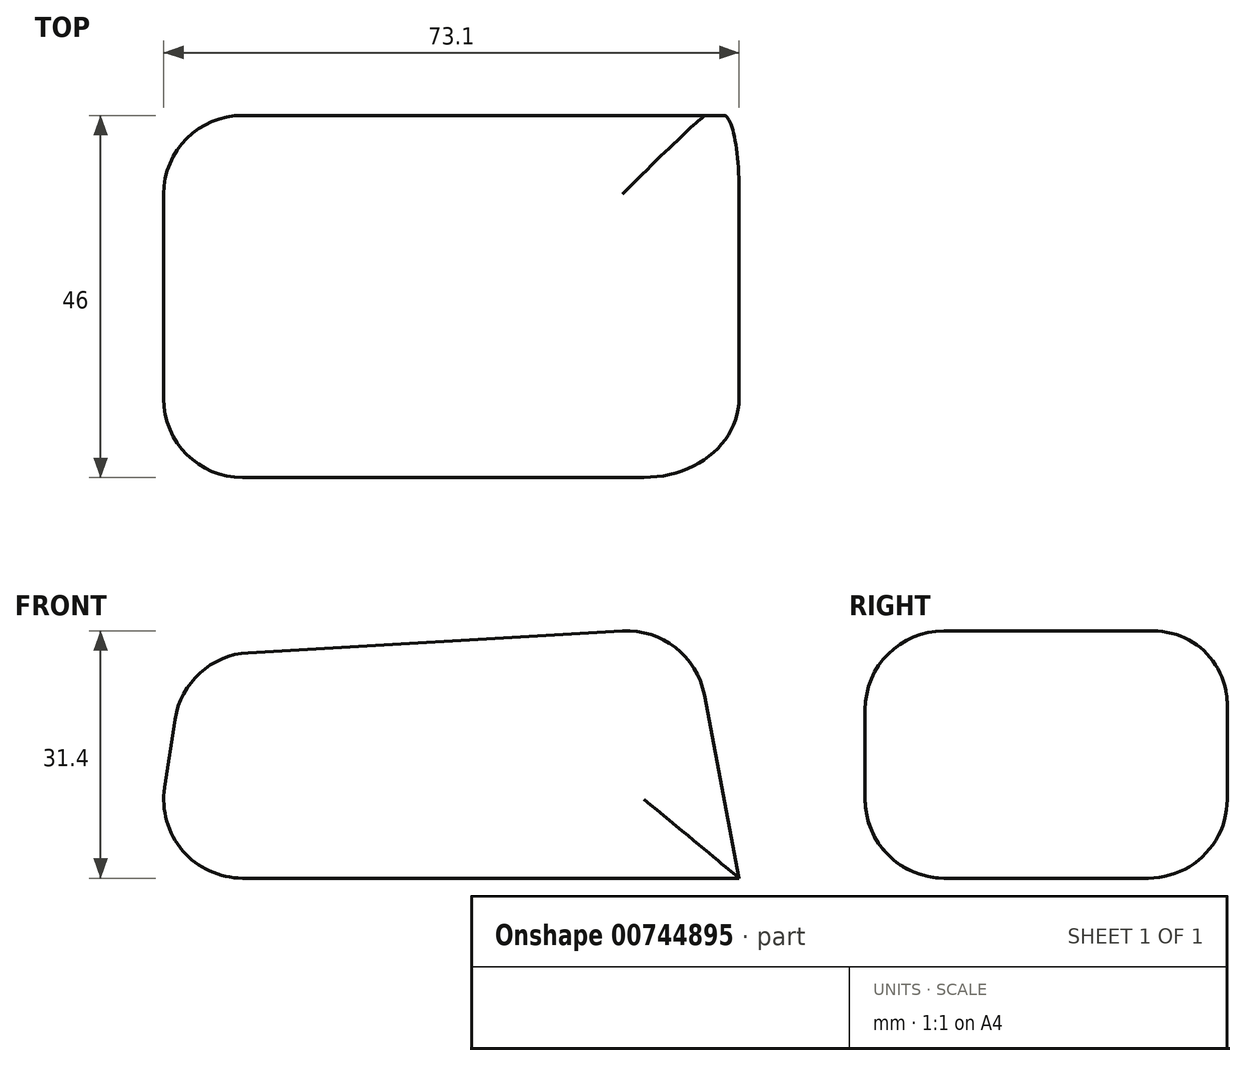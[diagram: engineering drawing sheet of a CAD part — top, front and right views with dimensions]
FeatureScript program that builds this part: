
annotation { "Feature Type Name" : "Feature", "Feature Type Description" : "" }
export const myFeature = defineFeature(function(context is Context, id is Id, definition is map)
    precondition{}
    {
        {
            var Q0;
            Q0=qCreatedBy(makeId("Front.planeOp"),FACE);
            var sketch = newSketch(context, id + "F0", { "sketchPlane" : qUnion([Q0])});
            skLineSegment(sketch, "E0", {"start": v(-36.49, 41.28) * mm, "end": v(27.88, 45) * mm});
            skLineSegment(sketch, "E1", {"start": v(27.88, 45) * mm, "end": v(33.95, 13.1) * mm});
            skLineSegment(sketch, "E2", {"start": v(33.95, 13.1) * mm, "end": v(-40.8, 13.1) * mm});
            skLineSegment(sketch, "E3", {"start": v(-40.8, 13.1) * mm, "end": v(-36.49, 41.28) * mm});
            skSolve(sketch);
        }
        {
            var Q0;
            Q0=makeQuery(id+"F0.imprint","IMPRINT",FACE,{"disambiguationData":[TD([[makeQuery(id+"F0.imprint","IMPRINT",EDGE,{"derivedFrom":sQuery(id+"F0.wireOp",EDGE,"E0")}),-1.0]])]});
            extrude(context, id + "F1", {"entities" : qUnion([Q0]), "depth" : 46 * mm, "offsetDistance" : 25 * mm});
        }
        {
            var Q0;
            Q0=makeQuery(id+"F1.opExtrude","SWEPT_FACE",FACE,{"disambiguationData":[OSD([sQuery(id+"F0.wireOp",EDGE,"E0")])]});
            var Q1;
            Q1=makeQuery(id+"F1.opExtrude","CAP_EDGE",EDGE,{"disambiguationData":[OSD([sQuery(id+"F0.wireOp",EDGE,"E0")])],"isStart":false});
            var Q2;
            Q2=makeQuery(id+"F1.opExtrude","CAP_EDGE",EDGE,{"disambiguationData":[OSD([sQuery(id+"F0.wireOp",EDGE,"E2")])],"isStart":true});
            var Q3;
            Q3=makeQuery(id+"F1.opExtrude","SWEPT_EDGE",EDGE,{"disambiguationData":[OSD([sQuery(id+"F0.wireOp",EDGE,"E2"),sQuery(id+"F0.wireOp",EDGE,"E3")])]});
            var Q4;
            Q4=makeQuery(id+"F1.opExtrude","CAP_EDGE",EDGE,{"disambiguationData":[OSD([sQuery(id+"F0.wireOp",EDGE,"E3")])],"isStart":true});
            var Q5;
            Q5=makeQuery(id+"F1.opExtrude","CAP_FACE",FACE,{"disambiguationData":[OSD([sQuery(id+"F0.wireOp",EDGE,"E0"),sQuery(id+"F0.wireOp",EDGE,"E1"),sQuery(id+"F0.wireOp",EDGE,"E2"),sQuery(id+"F0.wireOp",EDGE,"E3")])],"isStart":false});
            fillet(context, id + "F2", {"entities" : qUnion([Q0, Q1, Q2, Q3, Q4, Q5]), "radius" : 10 * mm, "tangentPropagation" : true, "allowEdgeOverflow" : false});
        }
    });
